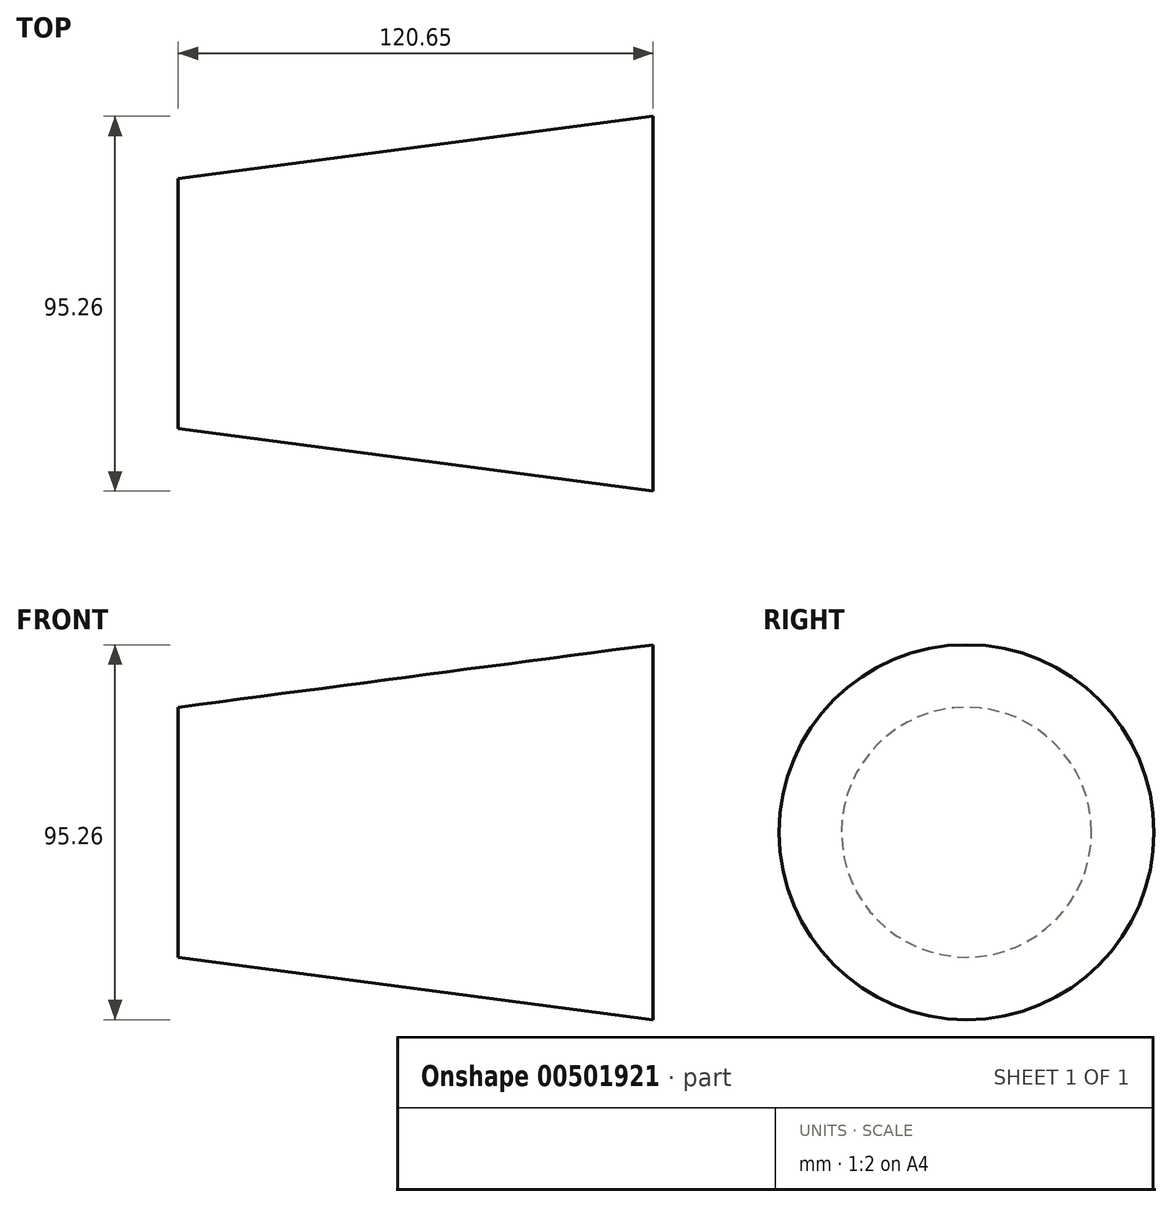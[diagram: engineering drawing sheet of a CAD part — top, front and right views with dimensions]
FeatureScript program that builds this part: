
annotation { "Feature Type Name" : "Feature", "Feature Type Description" : "" }
export const myFeature = defineFeature(function(context is Context, id is Id, definition is map)
    precondition{}
    {
        {
            var Q0;
            Q0=qCreatedBy(makeId("Front.planeOp"),FACE);
            var sketch = newSketch(context, id + "F0", { "sketchPlane" : qUnion([Q0])});
            skLineSegment(sketch, "E0", {"start": v(0, 0) * mm, "end": v(0, 63.5) * mm});
            skLineSegment(sketch, "E1", {"start": v(120.65, 79.38) * mm, "end": v(120.65, -15.88) * mm});
            skLineSegment(sketch, "E2", {"start": v(120.65, 79.37) * mm, "end": v(0, 63.5) * mm});
            skLineSegment(sketch, "E3", {"start": v(0, 0) * mm, "end": v(120.65, -15.88) * mm});
            skLineSegment(sketch, "E4", {"start": v(0, 31.75) * mm, "end": v(120.65, 31.75) * mm});
            skSolve(sketch);
        }
        {
            var Q0;
            {var subQ0=sQuery(id+"F0.wireOp",EDGE,"E3");Q0=makeQuery(id+"F0.imprint","IMPRINT",FACE,{"disambiguationData":[TD([[makeQuery(id+"F0.imprint","IMPRINT",EDGE,{"derivedFrom":subQ0}),1.0]])]});}
            var Q1;
            Q1=sQuery(id+"F0.wireOp",EDGE,"E4");
            revolve(context, id + "F1", {"entities" : qUnion([Q0]), "axis" : qUnion([Q1]), "revolveType" : RevolveType.FULL});
        }
    });
